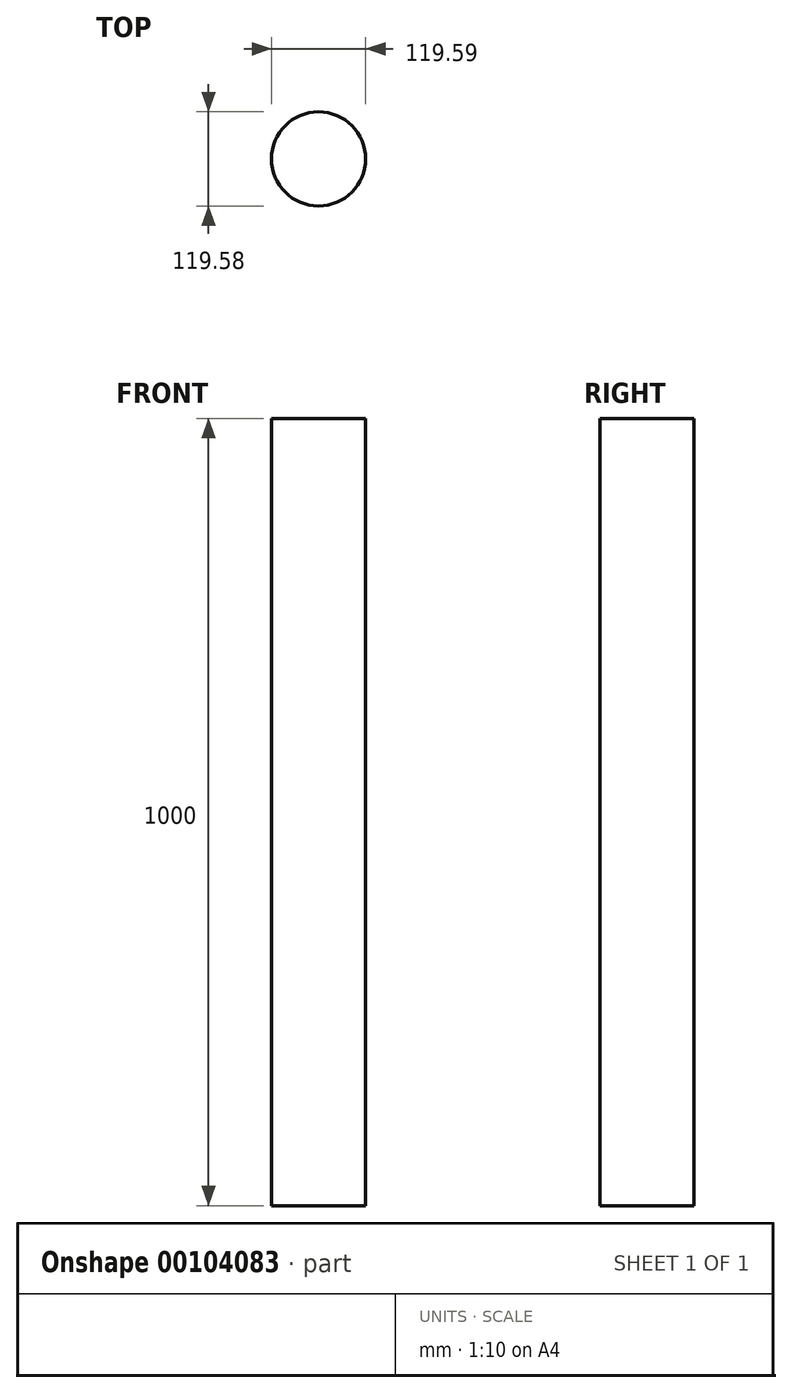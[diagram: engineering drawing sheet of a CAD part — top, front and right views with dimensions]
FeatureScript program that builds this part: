
annotation { "Feature Type Name" : "Feature", "Feature Type Description" : "" }
export const myFeature = defineFeature(function(context is Context, id is Id, definition is map)
    precondition{}
    {
        {
            var Q0;
            Q0=qCreatedBy(makeId("Top.planeOp"),FACE);
            var sketch = newSketch(context, id + "F0", { "sketchPlane" : qUnion([Q0])});
            skCircle(sketch, "E0", {"center": v(-0.18, -0.1) * mm, "radius": 59.8 * mm});
            skSolve(sketch);
        }
        {
            var Q0;
            Q0=makeQuery(id+"F0.imprint","IMPRINT",FACE,{"disambiguationData":[TD([[makeQuery(id+"F0.imprint","IMPRINT",EDGE,{"derivedFrom":sQuery(id+"F0.wireOp",EDGE,"E0")}),1.0]])]});
            extrude(context, id + "F1", {"entities" : qUnion([Q0]), "depth" : 1000 * mm});
        }
    });
